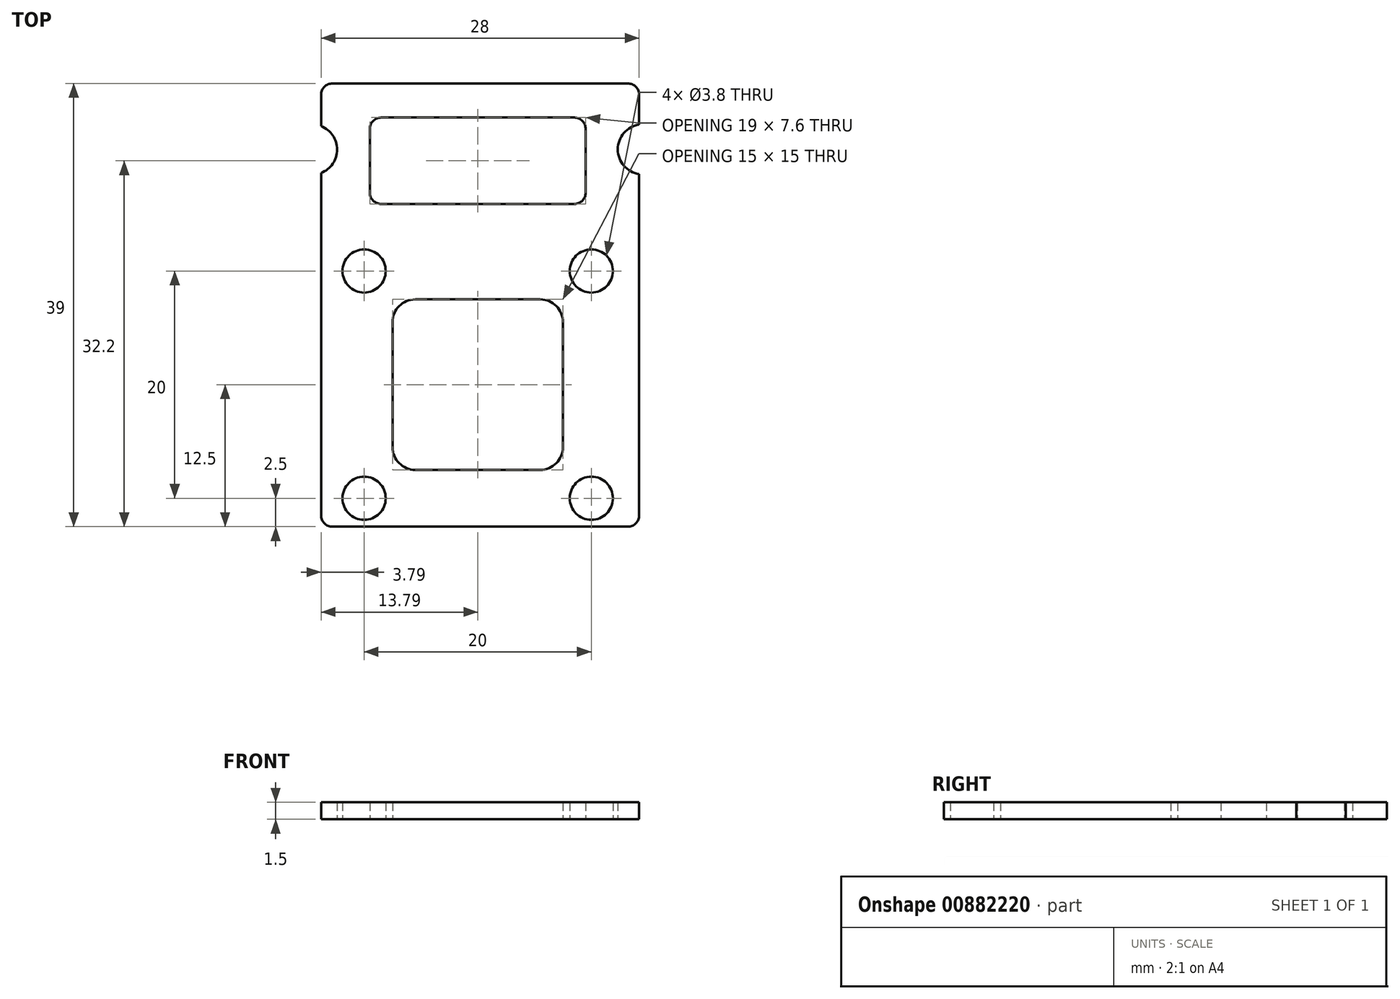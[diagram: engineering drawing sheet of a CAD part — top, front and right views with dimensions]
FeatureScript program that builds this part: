
annotation { "Feature Type Name" : "Feature", "Feature Type Description" : "" }
export const myFeature = defineFeature(function(context is Context, id is Id, definition is map)
    precondition{}
    {
        {
            var Q0;
            Q0=qCreatedBy(makeId("Top.planeOp"),FACE);
            var sketch = newSketch(context, id + "F0", { "sketchPlane" : qUnion([Q0])});
            skLineSegment(sketch, "E0.bottom", {"start": v(-12.79, 0) * mm, "end": v(13.21, 0) * mm});
            skLineSegment(sketch, "E0.top", {"start": v(-12.79, 39) * mm, "end": v(13.21, 39) * mm});
            skLineSegment(sketch, "E0.left", {"start": v(-13.79, 1) * mm, "end": v(-13.79, 31.13) * mm});
            skLineSegment(sketch, "E0.right", {"start": v(14.21, 1) * mm, "end": v(14.21, 31.02) * mm});
            skLineSegment(sketch, "E1.bottom", {"start": v(5.5, 5) * mm, "end": v(-5.5, 5) * mm});
            skLineSegment(sketch, "E1.top", {"start": v(5.5, 20) * mm, "end": v(-5.5, 20) * mm});
            skLineSegment(sketch, "E1.left", {"start": v(7.5, 7) * mm, "end": v(7.5, 18) * mm});
            skLineSegment(sketch, "E1.right", {"start": v(-7.5, 7) * mm, "end": v(-7.5, 18) * mm});
            skPoint(sketch, "E1.middle", {"position": v(0, 12.5) * mm});
            skCircle(sketch, "E2", {"center": v(-10, 22.5) * mm, "radius": 1.9 * mm});
            skCircle(sketch, "E3", {"center": v(10, 22.5) * mm, "radius": 1.9 * mm});
            skCircle(sketch, "E4", {"center": v(10, 2.5) * mm, "radius": 1.9 * mm});
            skCircle(sketch, "E5", {"center": v(-10, 2.5) * mm, "radius": 1.9 * mm});
            skPoint(sketch, "E6.startSnap0", {"position": v(0.21, 39) * mm});
            skLineSegment(sketch, "E7.bottom", {"start": v(8.5, 28.4) * mm, "end": v(-8.5, 28.4) * mm});
            skLineSegment(sketch, "E7.top", {"start": v(8.5, 36) * mm, "end": v(-8.5, 36) * mm});
            skLineSegment(sketch, "E7.left", {"start": v(9.5, 29.4) * mm, "end": v(9.5, 35) * mm});
            skLineSegment(sketch, "E7.right", {"start": v(-9.5, 29.4) * mm, "end": v(-9.5, 35) * mm});
            skPoint(sketch, "E7.middle", {"position": v(0, 32.2) * mm});
            skArc(sketch, "E8", {"start": v(-13.79, 31.13) * mm, "mid": v(-12.37, 33.19) * mm, "end": v(-13.79, 35.24) * mm});
            skArc(sketch, "E9", {"start": v(14.21, 35.37) * mm, "mid": v(12.33, 33.2) * mm, "end": v(14.21, 31.02) * mm});
            skLineSegment(sketch, "E10.trimOffspring", {"start": v(-13.79, 35.24) * mm, "end": v(-13.79, 38) * mm});
            skLineSegment(sketch, "E11.trimOffspring", {"start": v(14.21, 35.37) * mm, "end": v(14.21, 38) * mm});
            skPoint(sketch, "E12.orphan", {"position": v(0, 39) * mm});
            skPoint(sketch, "E13.visualSharp", {"position": v(-9.5, 36) * mm});
            skArc(sketch, "E13.filletArc", {"start": v(-8.5, 36) * mm, "mid": v(-9.2, 35.7) * mm, "end": v(-9.5, 35) * mm});
            skPoint(sketch, "E14.visualSharp", {"position": v(9.5, 36) * mm});
            skArc(sketch, "E14.filletArc", {"start": v(9.5, 35) * mm, "mid": v(9.2, 35.7) * mm, "end": v(8.5, 36) * mm});
            skPoint(sketch, "E15.visualSharp", {"position": v(-9.5, 28.4) * mm});
            skArc(sketch, "E15.filletArc", {"start": v(-9.5, 29.4) * mm, "mid": v(-9.2, 28.7) * mm, "end": v(-8.5, 28.4) * mm});
            skPoint(sketch, "E16.visualSharp", {"position": v(9.5, 28.4) * mm});
            skArc(sketch, "E16.filletArc", {"start": v(8.5, 28.4) * mm, "mid": v(9.2, 28.7) * mm, "end": v(9.5, 29.4) * mm});
            skPoint(sketch, "E17.visualSharp", {"position": v(-13.79, 39) * mm});
            skArc(sketch, "E17.filletArc", {"start": v(-12.79, 39) * mm, "mid": v(-13.5, 38.7) * mm, "end": v(-13.79, 38) * mm});
            skPoint(sketch, "E18.visualSharp", {"position": v(14.21, 39) * mm});
            skArc(sketch, "E18.filletArc", {"start": v(14.21, 38) * mm, "mid": v(13.92, 38.7) * mm, "end": v(13.21, 39) * mm});
            skPoint(sketch, "E19.visualSharp", {"position": v(14.21, 0) * mm});
            skArc(sketch, "E19.filletArc", {"start": v(13.21, 0) * mm, "mid": v(13.92, 0.3) * mm, "end": v(14.21, 1) * mm});
            skPoint(sketch, "E20.visualSharp", {"position": v(-13.79, 0) * mm});
            skArc(sketch, "E20.filletArc", {"start": v(-13.79, 1) * mm, "mid": v(-13.5, 0.3) * mm, "end": v(-12.79, 0) * mm});
            skPoint(sketch, "E21.visualSharp", {"position": v(-7.5, 20) * mm});
            skArc(sketch, "E21.filletArc", {"start": v(-5.5, 20) * mm, "mid": v(-6.91, 19.41) * mm, "end": v(-7.5, 18) * mm});
            skPoint(sketch, "E22.visualSharp", {"position": v(7.5, 20) * mm});
            skArc(sketch, "E22.filletArc", {"start": v(7.5, 18) * mm, "mid": v(6.91, 19.41) * mm, "end": v(5.5, 20) * mm});
            skPoint(sketch, "E23.visualSharp", {"position": v(7.5, 5) * mm});
            skArc(sketch, "E23.filletArc", {"start": v(5.5, 5) * mm, "mid": v(6.91, 5.59) * mm, "end": v(7.5, 7) * mm});
            skPoint(sketch, "E24.visualSharp", {"position": v(-7.5, 5) * mm});
            skArc(sketch, "E24.filletArc", {"start": v(-7.5, 7) * mm, "mid": v(-6.91, 5.59) * mm, "end": v(-5.5, 5) * mm});
            skSolve(sketch);
        }
        {
            var Q0;
            Q0=makeQuery(id+"F0.imprint","IMPRINT",FACE,{"disambiguationData":[TD([[makeQuery(id+"F0.imprint","IMPRINT",EDGE,{"derivedFrom":sQuery(id+"F0.wireOp",EDGE,"E0.bottom")}),1.0]])]});
            extrude(context, id + "F1", {"entities" : qUnion([Q0]), "depth" : 1.5 * mm, "offsetDistance" : 25 * mm});
        }
    });
